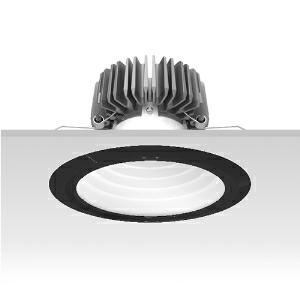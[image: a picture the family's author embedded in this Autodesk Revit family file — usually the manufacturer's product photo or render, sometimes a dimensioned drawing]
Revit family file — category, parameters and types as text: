
# Revit family: 3f_filippi_-_3f_reno_bianco_ampio_3f_filippi_-_30679_a01026_-_3f_reno_200_wh_3000-840_dali_wide___vt_bk_c398
name_source: partatom
category: Lighting Fixtures
units: mm (PartAtom-declared; Revit-internal decimal feet)

## family parameters
Cut with Voids When Loaded = No
Host = Face
Light Source = No
Part Type = Normal
Room Calculation Point = No
Round Connector Dimension = Use Diameter
Shared = No

## types (1)
- 3F Filippi - 3F Reno Bianco Ampio (1 x LED, 2529 lm, 28 W, 4000 K)
    Apparent Load = 28 VA
    Approval mark = CE
    CIE Flux Codes = 75 94 99 100 100
    Color Rendering = 80
    Color Temperature = 4000 K
    Control Gear = Electronic transformer
    Default Elevation = 1800 mm
    Description = ILLUMINOTECHNICAL
Luminous efficiency 100% (DLOR 100%, ULOR 0%).
Initial luminous flux of the luminaire 2529 lm.
Direct symmetric wide distribution.
Installation Interdistance Transv.D = 1.56 x hu - Long.D = 1.56 x hu.
Tabular UGR (CIE 117 - 4H-8H; S=0.25H; 70/50/20): RUG 21.8 - 21.7.
Beam angle: 74° - 74°.
Luminous efficacy 90 lm/W.
Lifetime (L90/B10): 30000 h. (tq+25°C)
Lifetime (L85/B10): 50000 h. (tq+25°C)
Lifetime (L70/B10): 80000 h. (tq+25°C)
Sudden decreased luminous flux after 50000 hours: 0% (C0).
Photobiological safety in compliance with IEC/TR 62778: RG0 risk exempt, (IEC 62471).
In compliance with IEC/EN 62722-2-1 - IEC/EN 62717 standards.

SOURCE
Compact LED module 3000/840.
Energy efficiency class (UE 2019/2020 - UE 2019/2015): E.
CIE 13.3 Colour rendering index: CRI >80 (R9 <50%).
IES TM-30 Fidelity Index: Rf = 84 Rg = 95.
CCT nominal colour temperature 4000 K.
Colour initial tolerance (MacAdam): SDCM 3.
Zhaga Book 3 compliant.

MECHANICAL
Passive heat dissipator in die-casting aluminium, oversized, for optimum thermal management of the LED module.
Parabolic element with graduated/concentric rings in white polycarbonate.
Transparent external lens with glossy and satin differentiated surfaces, with a cooling and anti-insect system in methacrylate (PMMA).
Fastening spring clips in stainless steel.
Dimensions: diameter 226 mm, height 146 mm. Weight 1.755 kg.
IP44 protection degree for exposed part, IP20 for recessed part.
Mechanical strength to impacts IK06 (1 joule).
Glow-wire test resistance 650°C.

ELECTRICAL
Wiring on a separate unit.
Halogen Free DALI-2 DATI (Parts 251, 252, 253), PUSH-DIM, electronic wiring 230V-50/60Hz, power factor 0.97 at full load, THD <25%, constant output current, SELV, class II, 1 driver, 1 DALI addresse.
Power of the luminaire 28 W.
ENEC - CE.
SAFE FLICKER: PstLM=<1 and SVM=<0.4 (IEC TR 61547-1 and IEC TR 63158), to ensure a more comfortable and safe light.
Luminaire compliant with EN 60598-2-22 for power supply from a centralised emergency system CPSS (Central Power Supply System), not incorporated in the luminaire - high risk areas excluded. The default power and flux are 100% in AC and 100% in DC.
Ambient temperature from 0°C to +25°C.
Temperature class T6 max 85°C.
Relative humidity UR: <85%.

INSTALLATION
Pull-up recessed fitting.
False ceiling carving: 200 mm.
All accessories dedicated to this product are available on the Catalog and on our website www.3F-Filippi.com.

ACCESSORIES
A01026 - VT transparent glass, tempered, not flammable, locked and in line with the trim, in black polycarbonate.

APPLICATIONS
Environments: architectural, commercial, exhibition areas, transit areas, corridors, shops, display windows, service areas.
In false ceilings with narrow voids.

LIGHT MANAGEMENT
Recommended minimum setting: 10%.
The luminaire, equipped with (DALI-2 DATI) driver, can be controlled manually with 3F Easy Dim technology or automatically/manually with wired or wireless DALI/D2D control systems.
The D2D driver guarantees interoperability with other devices with the same certification by making the following information available:
Device Data (Part 251), Energy Report (Part 252), Diagnosis & Maintenance (Part 253).
In electrical systems without a regulation system (manual or automatic) and DALI bus, a suitable jumper must be made on the DA-DA terminals of the appliance.

WARNING
Luminaire designed for disposal/recycling at end-of-life.
Replaceable (LED only) light source by a professional. Replaceable control gear by a professional.
    Height = 0 mm  [stored 0 ft]
    Lamp = 1 x LED
    Lamp Light Flux = 2529 lm
    Lamp Power = 28 W
    Lamp count = 1
    Length = 226 mm
    Lifetime = 50000 h
    Luminous efficacy = 90 lm/W
    Manufacturer = 3F Filippi
    ModVariant = No
    Model = 3F Filippi - 30679+A01026 - 3F Reno 200 WH 3000-840 DALI WIDE + VT BK
    Mounting Place = Ceiling
    Mounting Type = Recessed
    Number of Poles = 1
    OnlyDefault = Yes
    Power Factor = 1
    Product Name = 3F Filippi - 3F Reno Bianco Ampio
    Product group = recessed luminaire
    ProductGroupID = 4
    Protection Class = Protection class II
    Protection Degree = IP 20
    RLX_Detail_Level = 1
    RLX_Emergency_Light_Flux = 0 lm
    RLX_Emergency_Type = 0
    RLX_Emergency_Type_DB = No
    RlxData = <blob elided: 103233 chars, md5=10a01b19>
    Socket = socket
    Standby Power = 0 W
    System Light Flux = 2529 lm
    System Power = 28 W
    Type Comments = Product without accessories
    Type Image = 3ffilippi_3f_reno_200_wh__a01026.jpg
    URL = http://relux.com
    VarID = ---
    Voltage = 0 V
    Weight = 0.00 kg
    Width = 0 mm  [stored 0 ft]

note: [stored X ft] marks values corroborated as IEEE doubles in the binary element streams (Revit-internal decimal feet)

## geometry (parser evidence)
native form markers: Blend x4, Sweep x9
no freeform markers — native parametric forms only
